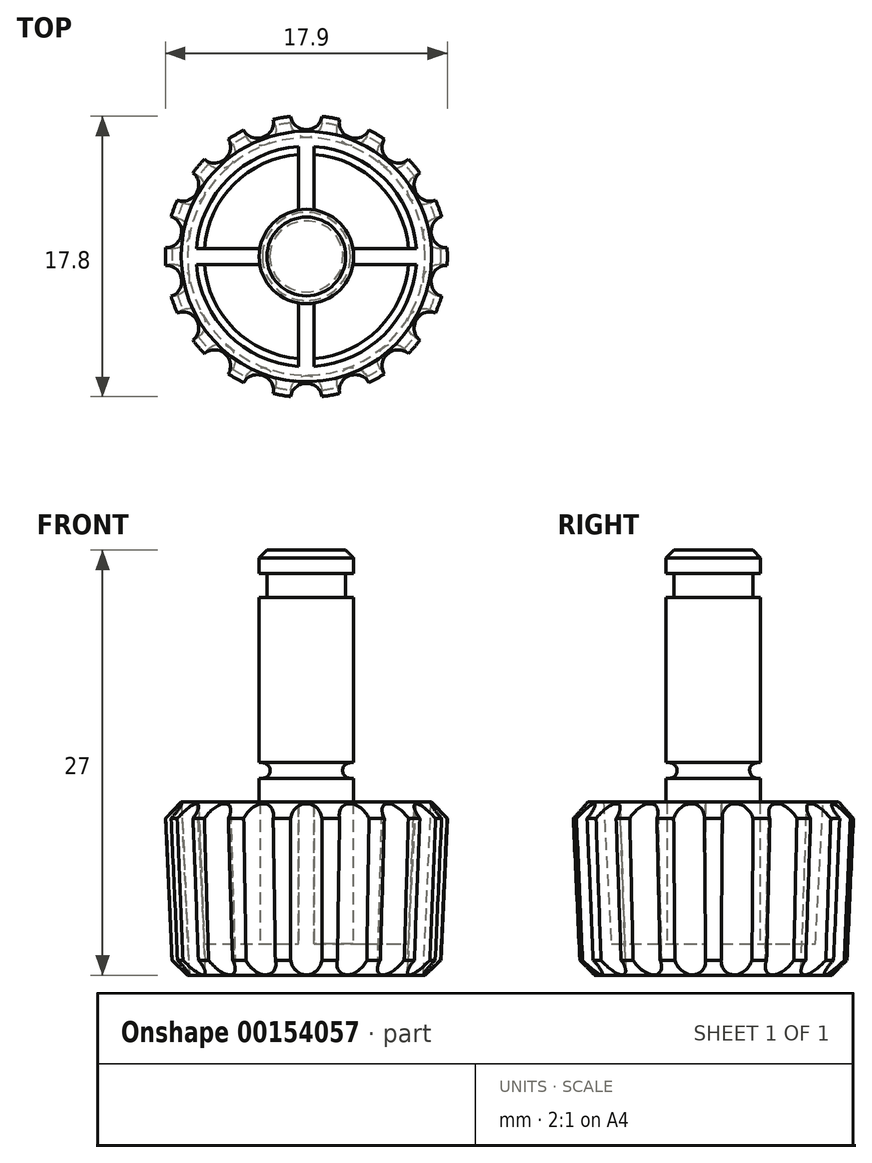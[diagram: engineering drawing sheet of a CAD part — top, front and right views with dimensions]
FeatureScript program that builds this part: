
annotation { "Feature Type Name" : "Feature", "Feature Type Description" : "" }
export const myFeature = defineFeature(function(context is Context, id is Id, definition is map)
    precondition{}
    {
        {
            var Q0;
            Q0=qCreatedBy(makeId("Top.planeOp"),FACE);
            var sketch = newSketch(context, id + "F0", { "sketchPlane" : qUnion([Q0])});
            skCircle(sketch, "E0", {"center": v(0, 0) * mm, "radius": 3 * mm});
            skSolve(sketch);
        }
        {
            var Q0;
            Q0 = qSketchRegion(id + "F0", true);
            extrude(context, id + "F1", {"entities" : qUnion([Q0]), "flatOperationType" : FlatOperationType.REMOVE, "offsetDistance" : 25 * mm, "depth" : 16 * mm, "hasSecondDirection" : true, "secondDirectionOppositeDirection" : true, "secondDirectionDepth" : 10 * mm, "domain" : OperationDomain.MODEL});
        }
        {
            var Q0;
            Q0=makeQuery(id+"F1.opExtrude","CAP_EDGE",EDGE,{"disambiguationData":[OSD([sQuery(id+"F0.wireOp",EDGE,"E0")])],"isStart":false});
            chamfer(context, id + "F2", {"entities" : qUnion([Q0]), "width" : 0.5 * mm});
        }
        {
            var Q0;
            Q0=qCreatedBy(makeId("Right.planeOp"),FACE);
            var sketch = newSketch(context, id + "F3", { "sketchPlane" : qUnion([Q0])});
            skLineSegment(sketch, "E1.bottom", {"start": v(-8, 0) * mm, "end": v(8, 0) * mm});
            skLineSegment(sketch, "E1.top", {"start": v(-8, -10) * mm, "end": v(8, -10) * mm});
            skLineSegment(sketch, "E1.left", {"start": v(-8, 0) * mm, "end": v(-8, -10) * mm});
            skLineSegment(sketch, "E1.right", {"start": v(8, 0) * mm, "end": v(8, -10) * mm});
            skLineSegment(sketch, "E2", {"start": v(0, 0) * mm, "end": v(0, -27.67) * mm, "construction": true});
            skSolve(sketch);
        }
        {
            var Q0;
            Q0=makeQuery(id+"F3.imprint","IMPRINT",FACE,{"disambiguationData":[TD([[makeQuery(id+"F3.imprint","IMPRINT",EDGE,{"derivedFrom":sQuery(id+"F3.wireOp",EDGE,"E1.bottom")}),-1.0]])]});
            extrude(context, id + "F4", {"entities" : qUnion([Q0]), "operationType" : NewBodyOperationType.ADD, "flatOperationType" : FlatOperationType.REMOVE, "offsetDistance" : 25 * mm, "depth" : 1 * mm, "domain" : OperationDomain.MODEL, "symmetric" : true});
        }
        {
            var Q0;
            Q0=qCreatedBy(makeId("Front.planeOp"),FACE);
            var sketch = newSketch(context, id + "F5", { "sketchPlane" : qUnion([Q0])});
            skLineSegment(sketch, "E3.bottom", {"start": v(-7.5, 0) * mm, "end": v(8.5, 0) * mm});
            skLineSegment(sketch, "E3.top", {"start": v(-7.5, -10) * mm, "end": v(8.5, -10) * mm});
            skLineSegment(sketch, "E3.left", {"start": v(-7.5, 0) * mm, "end": v(-7.5, -10) * mm});
            skLineSegment(sketch, "E3.right", {"start": v(8.5, 0) * mm, "end": v(8.5, -10) * mm});
            skSolve(sketch);
        }
        {
            var Q0;
            Q0=makeQuery(id+"F5.imprint","IMPRINT",FACE,{"disambiguationData":[TD([[makeQuery(id+"F5.imprint","IMPRINT",EDGE,{"derivedFrom":sQuery(id+"F5.wireOp",EDGE,"E3.bottom")}),-1.0]])]});
            extrude(context, id + "F6", {"entities" : qUnion([Q0]), "operationType" : NewBodyOperationType.ADD, "flatOperationType" : FlatOperationType.REMOVE, "offsetDistance" : 25 * mm, "depth" : 1 * mm, "domain" : OperationDomain.MODEL, "symmetric" : true});
        }
        {
            var Q0;
            Q0=qCreatedBy(makeId("Right.planeOp"),FACE);
            var sketch = newSketch(context, id + "F7", { "sketchPlane" : qUnion([Q0])});
            skLineSegment(sketch, "E4", {"start": v(9, 0) * mm, "end": v(8.5, -11) * mm});
            skLineSegment(sketch, "E5", {"start": v(8.5, -11) * mm, "end": v(0, -11) * mm});
            skLineSegment(sketch, "E6", {"start": v(0, -11) * mm, "end": v(0, -9) * mm});
            skLineSegment(sketch, "E7", {"start": v(0, -9) * mm, "end": v(6.5, -9) * mm});
            skLineSegment(sketch, "E8", {"start": v(6.5, -9) * mm, "end": v(7, 0) * mm});
            skLineSegment(sketch, "E9", {"start": v(7, 0) * mm, "end": v(9, 0) * mm});
            skLineSegment(sketch, "E10", {"start": v(0, -15.87) * mm, "end": v(0, 18.3) * mm, "construction": true});
            skSolve(sketch);
        }
        {
            var Q0;
            Q0 = qSketchRegion(id + "F7", true);
            var Q1;
            Q1=sQuery(id+"F7.wireOp",EDGE,"E10");
            revolve(context, id + "F8", {"operationType" : NewBodyOperationType.ADD, "surfaceOperationType" : NewSurfaceOperationType.NEW, "entities" : qUnion([Q0]), "axis" : qUnion([Q1]), "revolveType" : RevolveType.FULL});
        }
        {
            var Q0;
            Q0=makeQuery(id+"F8.opRevolve","SWEPT_EDGE",EDGE,{"disambiguationData":[OSD([sQuery(id+"F7.wireOp",EDGE,"E4"),sQuery(id+"F7.wireOp",EDGE,"E5")])]});
            chamfer(context, id + "F9", {"entities" : qUnion([Q0]), "width" : 1 * mm, "tangentPropagation" : true});
        }
        {
            var Q0;
            Q0=makeQuery(id+"F8.opRevolve","SWEPT_EDGE",EDGE,{"disambiguationData":[OSD([sQuery(id+"F7.wireOp",EDGE,"E4"),sQuery(id+"F7.wireOp",EDGE,"E9")])]});
            chamfer(context, id + "F10", {"entities" : qUnion([Q0]), "width" : 1 * mm, "tangentPropagation" : true});
        }
        {
            var Q0;
            Q0=qCreatedBy(makeId("Right.planeOp"),FACE);
            var sketch = newSketch(context, id + "F11", { "sketchPlane" : qUnion([Q0])});
            skLineSegment(sketch, "E11", {"start": v(9.12, 2.58) * mm, "end": v(8.36, -14.12) * mm});
            skPoint(sketch, "E12.center", {"position": v(0, 0) * mm});
            skSolve(sketch);
        }
        {
            var Q0;
            Q0=qCreatedBy(makeId("Top.planeOp"),FACE);
            var sketch = newSketch(context, id + "F12", { "sketchPlane" : qUnion([Q0])});
            skCircle(sketch, "E13", {"center": v(0, 9.06) * mm, "radius": 1 * mm});
            skCircle(sketch, "E14.1.0", {"center": v(-3.1, 8.51) * mm, "radius": 1 * mm});
            skCircle(sketch, "E14.2.0", {"center": v(-5.82, 6.94) * mm, "radius": 1 * mm});
            skPoint(sketch, "E14.center", {"position": v(0, 0) * mm});
            skCircle(sketch, "E15.1.3.0", {"center": v(-7.85, 4.53) * mm, "radius": 1 * mm});
            skCircle(sketch, "E15.1.4.0", {"center": v(-8.92, 1.57) * mm, "radius": 1 * mm});
            skCircle(sketch, "E15.1.5.0", {"center": v(-8.92, -1.57) * mm, "radius": 1 * mm});
            skCircle(sketch, "E15.1.6.0", {"center": v(-7.85, -4.53) * mm, "radius": 1 * mm});
            skCircle(sketch, "E15.1.7.0", {"center": v(-5.82, -6.94) * mm, "radius": 1 * mm});
            skCircle(sketch, "E15.1.8.0", {"center": v(-3.1, -8.51) * mm, "radius": 1 * mm});
            skCircle(sketch, "E15.1.9.0", {"center": v(0, -9.06) * mm, "radius": 1 * mm});
            skCircle(sketch, "E15.1.10.0", {"center": v(3.1, -8.51) * mm, "radius": 1 * mm});
            skCircle(sketch, "E15.1.11.0", {"center": v(5.82, -6.94) * mm, "radius": 1 * mm});
            skCircle(sketch, "E15.1.12.0", {"center": v(7.85, -4.53) * mm, "radius": 1 * mm});
            skCircle(sketch, "E15.1.13.0", {"center": v(8.92, -1.57) * mm, "radius": 1 * mm});
            skCircle(sketch, "E15.1.14.0", {"center": v(8.92, 1.57) * mm, "radius": 1 * mm});
            skCircle(sketch, "E15.1.15.0", {"center": v(7.85, 4.53) * mm, "radius": 1 * mm});
            skCircle(sketch, "E15.1.16.0", {"center": v(5.82, 6.94) * mm, "radius": 1 * mm});
            skCircle(sketch, "E15.1.17.0", {"center": v(3.1, 8.51) * mm, "radius": 1 * mm});
            skSolve(sketch);
        }
        {
            var Q0;
            Q0=makeQuery(id+"F12.imprint","IMPRINT",FACE,{"disambiguationData":[TD([[makeQuery(id+"F12.imprint","IMPRINT",EDGE,{"derivedFrom":sQuery(id+"F12.wireOp",EDGE,"E13")}),1.0]])]});
            var Q1;
            Q1=sQuery(id+"F12.wireOp",EDGE,"E13");
            var Q2;
            Q2=sQuery(id+"F11.wireOp",EDGE,"E11");
            sweep(context, id + "F13", {"operationType" : NewBodyOperationType.REMOVE, "profiles" : qUnion([Q0]), "surfaceProfiles" : qUnion([Q1]), "path" : qUnion([Q2]), "keepProfileOrientation" : true});
        }
        {
            var Q0;
            Q0=makeQuery(id+"F1.opExtrude","SWEPT_BODY",BODY,{"disambiguationData":[OSD([sQuery(id+"F0.wireOp",EDGE,"E0")])]});
            var Q1;
            Q1=makeQuery(id+"F13.boolean.opBoolean","COPY",FACE,{"derivedFrom":makeQuery(id+"F13.opSweep","SWEPT_FACE",FACE,{"disambiguationData":[OSD([sQuery(id+"F11.wireOp",EDGE,"E11"),sQuery(id+"F12.wireOp",EDGE,"E13")])]})});
            var Q2;
            Q2=sQuery(id+"F7.wireOp",EDGE,"E10");
            circularPattern(context, id + "F14", {"patternType" : PatternType.FACE, "faces" : qUnion([Q1]), "axis" : qUnion([Q2]), "angle" : 20 * degree, "instanceCount" : 18});
        }
        {
            var Q0;
            Q0=qCreatedBy(makeId("Front.planeOp"),FACE);
            var sketch = newSketch(context, id + "F15", { "sketchPlane" : qUnion([Q0])});
            skLineSegment(sketch, "E16.bottom", {"start": v(-4, 14.5) * mm, "end": v(-2.5, 14.5) * mm});
            skLineSegment(sketch, "E16.top", {"start": v(-4, 13) * mm, "end": v(-2.5, 13) * mm});
            skLineSegment(sketch, "E16.left", {"start": v(-4, 14.5) * mm, "end": v(-4, 13) * mm});
            skArc(sketch, "E17", {"start": v(-2.8, 1.5) * mm, "mid": v(-2.3, 2) * mm, "end": v(-2.8, 2.5) * mm});
            skLineSegment(sketch, "E18", {"start": v(-2.8, 2.5) * mm, "end": v(-3.65, 2.51) * mm});
            skLineSegment(sketch, "E19", {"start": v(-3.64, 2.51) * mm, "end": v(-3.66, 1.51) * mm});
            skLineSegment(sketch, "E20", {"start": v(-3.66, 1.51) * mm, "end": v(-2.8, 1.5) * mm});
            skLineSegment(sketch, "E21", {"start": v(0, 19.03) * mm, "end": v(0, -15.2) * mm, "construction": true});
            skLineSegment(sketch, "E22", {"start": v(-2.5, 14.5) * mm, "end": v(-2.5, 13) * mm});
            skSolve(sketch);
        }
        {
            var Q0;
            Q0 = qSketchRegion(id + "F15", true);
            var Q1;
            Q1=sQuery(id+"F15.wireOp",EDGE,"E21");
            revolve(context, id + "F16", {"operationType" : NewBodyOperationType.REMOVE, "entities" : qUnion([Q0]), "axis" : qUnion([Q1]), "revolveType" : RevolveType.FULL, "oppositeDirection" : true});
        }
    });
